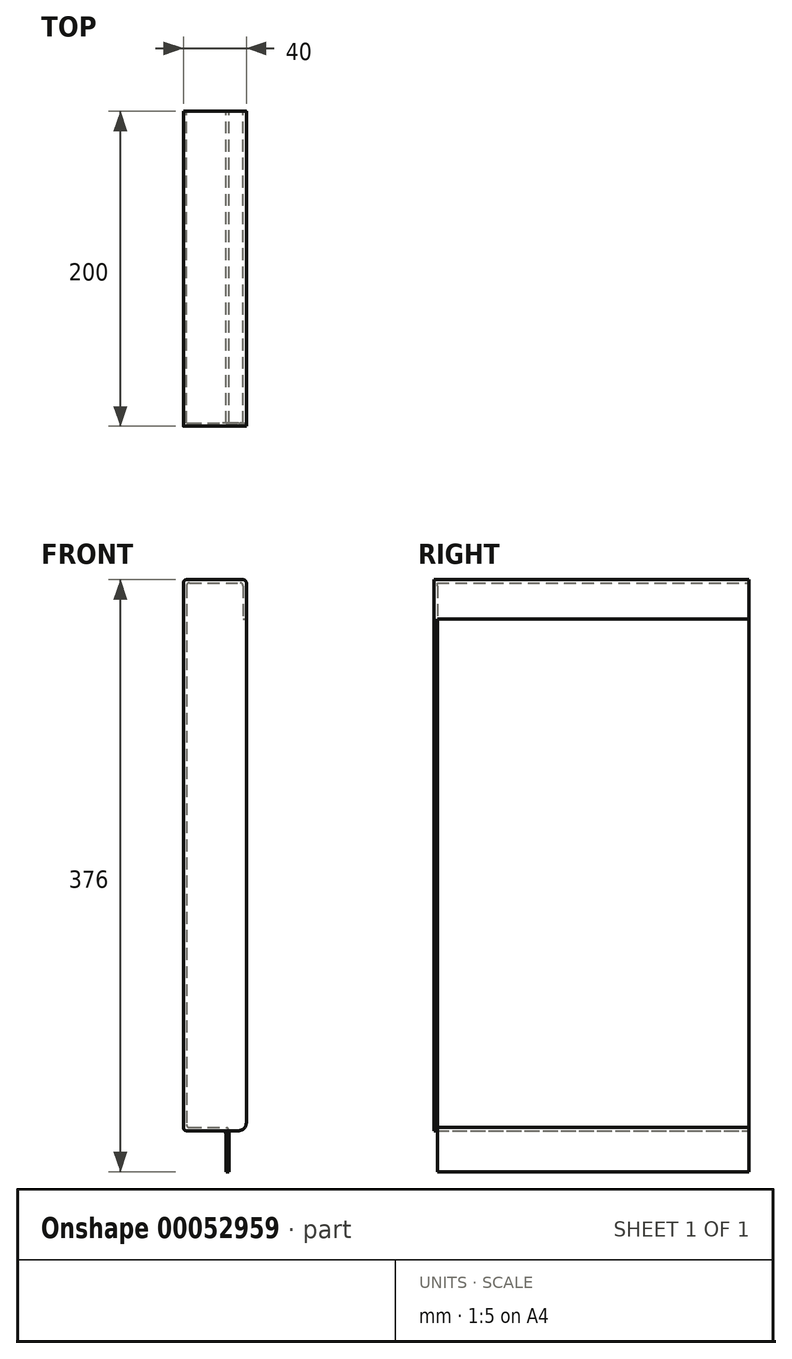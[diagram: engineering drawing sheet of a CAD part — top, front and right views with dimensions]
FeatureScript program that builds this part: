
annotation { "Feature Type Name" : "Feature", "Feature Type Description" : "" }
export const myFeature = defineFeature(function(context is Context, id is Id, definition is map)
    precondition{}
    {
        {
            var Q0;
            Q0=qCreatedBy(makeId("Front.planeOp"),FACE);
            var sketch = newSketch(context, id + "F0", { "sketchPlane" : qUnion([Q0])});
            skLineSegment(sketch, "E0", {"start": v(0, 0) * mm, "end": v(0, -350) * mm});
            skLineSegment(sketch, "E1", {"start": v(0, -350) * mm, "end": v(27, -350) * mm});
            skLineSegment(sketch, "E2", {"start": v(27, -350) * mm, "end": v(27, -376) * mm});
            skLineSegment(sketch, "E3", {"start": v(0, 0) * mm, "end": v(40, 0) * mm});
            skLineSegment(sketch, "E4", {"start": v(40, 0) * mm, "end": v(40, -25) * mm});
            skLineSegment(sketch, "E5.0", {"start": v(38, -2) * mm, "end": v(38, -25) * mm});
            skLineSegment(sketch, "E5.1", {"start": v(29, -348) * mm, "end": v(29, -376) * mm});
            skLineSegment(sketch, "E5.2", {"start": v(2, -348) * mm, "end": v(29, -348) * mm});
            skLineSegment(sketch, "E5.3", {"start": v(2, -2) * mm, "end": v(2, -348) * mm});
            skLineSegment(sketch, "E5.4", {"start": v(2, -2) * mm, "end": v(38, -2) * mm});
            skLineSegment(sketch, "E6", {"start": v(38, -25) * mm, "end": v(40, -25) * mm});
            skLineSegment(sketch, "E7", {"start": v(27, -376) * mm, "end": v(29, -376) * mm});
            skSolve(sketch);
        }
        {
            var Q0;
            Q0=qCreatedBy(makeId("Top.planeOp"),FACE);
            var sketch = newSketch(context, id + "F1", { "sketchPlane" : qUnion([Q0])});
            skLineSegment(sketch, "E8", {"start": v(0, 0) * mm, "end": v(0, 198) * mm});
            skSolve(sketch);
        }
        {
            var Q0;
            Q0=qSketchRegion(id+"F0",true);
            var Q1;
            Q1=qConstructionFilter(qBodyType(qCreatedBy(id+"F1",EDGE),BodyType.WIRE),ConstructionObject.NO);
            sweep(context, id + "F2", {"profiles" : qUnion([Q0]), "path" : qUnion([Q1])});
        }
        {
            var Q0;
            Q0=makeQuery(id+"F2.opSweep","CAP_FACE",FACE,{"disambiguationData":[OSD([sQuery(id+"F0.wireOp",EDGE,"E0"),sQuery(id+"F0.wireOp",EDGE,"E1"),sQuery(id+"F0.wireOp",EDGE,"E2"),sQuery(id+"F0.wireOp",EDGE,"E3"),sQuery(id+"F0.wireOp",EDGE,"E4"),sQuery(id+"F0.wireOp",EDGE,"E5.0"),sQuery(id+"F0.wireOp",EDGE,"E5.1"),sQuery(id+"F0.wireOp",EDGE,"E5.2"),sQuery(id+"F0.wireOp",EDGE,"E5.3"),sQuery(id+"F0.wireOp",EDGE,"E5.4"),sQuery(id+"F0.wireOp",EDGE,"E6"),sQuery(id+"F0.wireOp",EDGE,"E7"),sQuery(id+"F1.wireOp",VERTEX,"E8.start")])],"isStart":true});
            var sketch = newSketch(context, id + "F3", { "sketchPlane" : qUnion([Q0])});
            skLineSegment(sketch, "E9.0", {"start": v(40, 0) * mm, "end": v(0, 0) * mm});
            skLineSegment(sketch, "E10.0", {"start": v(0, -350) * mm, "end": v(0, 0) * mm});
            skPoint(sketch, "E11.0.end.orphan", {"position": v(27, -350) * mm});
            skPoint(sketch, "E12.0.start.orphan", {"position": v(40, -25) * mm});
            skLineSegment(sketch, "E13", {"start": v(40, 0) * mm, "end": v(40, -345) * mm});
            skLineSegment(sketch, "E14", {"start": v(35, -350) * mm, "end": v(0, -350) * mm});
            skPoint(sketch, "E15.visualSharp", {"position": v(40, -350) * mm});
            skArc(sketch, "E15.filletArc", {"start": v(35, -350) * mm, "mid": v(38.54, -348.54) * mm, "end": v(40, -345) * mm});
            skSolve(sketch);
        }
        {
            var Q0;
            Q0=qSketchRegion(id+"F3",true);
            extrude(context, id + "F4", {"entities" : qUnion([Q0]), "depth" : 2 * mm});
        }
        {
            var Q0;
            Q0=makeQuery(id+"F2.opSweep","SWEPT_BODY",BODY,{"disambiguationData":[OSD([sQuery(id+"F0.wireOp",EDGE,"E0"),sQuery(id+"F0.wireOp",EDGE,"E1"),sQuery(id+"F0.wireOp",EDGE,"E2"),sQuery(id+"F0.wireOp",EDGE,"E3"),sQuery(id+"F0.wireOp",EDGE,"E4"),sQuery(id+"F0.wireOp",EDGE,"E5.0"),sQuery(id+"F0.wireOp",EDGE,"E5.1"),sQuery(id+"F0.wireOp",EDGE,"E5.2"),sQuery(id+"F0.wireOp",EDGE,"E5.3"),sQuery(id+"F0.wireOp",EDGE,"E5.4"),sQuery(id+"F0.wireOp",EDGE,"E6"),sQuery(id+"F0.wireOp",EDGE,"E7"),sQuery(id+"F1.wireOp",EDGE,"E8")])]});
            var Q1;
            Q1=makeQuery(id+"F4.opExtrude","SWEPT_BODY",BODY,{"disambiguationData":[OSD([sQuery(id+"F3.wireOp",EDGE,"E9.0"),sQuery(id+"F3.wireOp",EDGE,"E10.0"),sQuery(id+"F3.wireOp",EDGE,"E13"),sQuery(id+"F3.wireOp",EDGE,"E14"),sQuery(id+"F3.wireOp",EDGE,"E15.filletArc")])]});
            booleanBodies(context, id + "F5", {"operationType" : BooleanOperationType.UNION, "tools" : qUnion([Q0, Q1])});
        }
        {
            var Q0;
            Q0=makeQuery(id+"F5.opBoolean","MERGE",EDGE,{"derivedFrom":[makeQuery(id+"F2.opSweep","SWEPT_EDGE",EDGE,{"disambiguationData":[OSD([sQuery(id+"F0.wireOp",EDGE,"E3"),sQuery(id+"F0.wireOp",EDGE,"E4"),sQuery(id+"F1.wireOp",EDGE,"E8")])]}),makeQuery(id+"F4.opExtrude","SWEPT_EDGE",EDGE,{"disambiguationData":[OSD([sQuery(id+"F3.wireOp",EDGE,"E9.0"),sQuery(id+"F3.wireOp",EDGE,"E13")])]})]});
            var Q1;
            Q1=makeQuery(id+"F5.opBoolean","MERGE",EDGE,{"derivedFrom":[makeQuery(id+"F2.opSweep","SWEPT_EDGE",EDGE,{"disambiguationData":[OSD([sQuery(id+"F0.wireOp",EDGE,"E0"),sQuery(id+"F0.wireOp",EDGE,"E3"),sQuery(id+"F1.wireOp",EDGE,"E8")])]}),makeQuery(id+"F4.opExtrude","SWEPT_EDGE",EDGE,{"disambiguationData":[OSD([sQuery(id+"F3.wireOp",EDGE,"E9.0"),sQuery(id+"F3.wireOp",EDGE,"E10.0")])]})]});
            var Q2;
            Q2=makeQuery(id+"F5.opBoolean","MERGE",EDGE,{"derivedFrom":[makeQuery(id+"F2.opSweep","SWEPT_EDGE",EDGE,{"disambiguationData":[OSD([sQuery(id+"F0.wireOp",EDGE,"E0"),sQuery(id+"F0.wireOp",EDGE,"E1"),sQuery(id+"F1.wireOp",EDGE,"E8")])]}),makeQuery(id+"F4.opExtrude","SWEPT_EDGE",EDGE,{"disambiguationData":[OSD([sQuery(id+"F3.wireOp",EDGE,"E10.0"),sQuery(id+"F3.wireOp",EDGE,"E14")])]})]});
            var Q3;
            Q3=makeQuery(id+"F2.opSweep","SWEPT_EDGE",EDGE,{"disambiguationData":[OSD([sQuery(id+"F0.wireOp",EDGE,"E5.1"),sQuery(id+"F0.wireOp",EDGE,"E5.2"),sQuery(id+"F1.wireOp",EDGE,"E8")])]});
            var Q4;
            Q4=makeQuery(id+"F2.opSweep","SWEPT_EDGE",EDGE,{"disambiguationData":[OSD([sQuery(id+"F0.wireOp",EDGE,"E1"),sQuery(id+"F0.wireOp",EDGE,"E2"),sQuery(id+"F1.wireOp",EDGE,"E8")])]});
            var Q5;
            Q5=makeQuery(id+"F2.opSweep","SWEPT_EDGE",EDGE,{"disambiguationData":[OSD([sQuery(id+"F0.wireOp",EDGE,"E5.2"),sQuery(id+"F0.wireOp",EDGE,"E5.3"),sQuery(id+"F1.wireOp",EDGE,"E8")])]});
            var Q6;
            Q6=makeQuery(id+"F2.opSweep","SWEPT_EDGE",EDGE,{"disambiguationData":[OSD([sQuery(id+"F0.wireOp",EDGE,"E5.3"),sQuery(id+"F0.wireOp",EDGE,"E5.4"),sQuery(id+"F1.wireOp",EDGE,"E8")])]});
            var Q7;
            Q7=makeQuery(id+"F2.opSweep","SWEPT_EDGE",EDGE,{"disambiguationData":[OSD([sQuery(id+"F0.wireOp",EDGE,"E5.0"),sQuery(id+"F0.wireOp",EDGE,"E5.4"),sQuery(id+"F1.wireOp",EDGE,"E8")])]});
            fillet(context, id + "F6", {"entities" : qUnion([Q0, Q1, Q2, Q3, Q4, Q5, Q6, Q7]), "radius" : 2 * mm, "tangentPropagation" : true, "allowEdgeOverflow" : false});
        }
    });
